# Revit family: Plumbing-Soap-Dispensers-Sloan-Valve-ESD-250
name_source: partatom
category: Specialty Equipment
units: mm (PartAtom-declared; Revit-internal decimal feet)

## family parameters
Cut with Voids When Loaded = No
Host = Face
OmniClass Number = 23.40.20.21.34
Part Type = Normal
Room Calculation Point = No
Round Connector Dimension = Use Diameter
Shared = No

## types (1)
- ESD-250-CP
    Assembly Code = D2010
    CW Connection = Yes
    Default Elevation = 0 "
    Depth = 5.38 "
    Description = Optima® Deck-Mounted Liquid Soap Dispenser, Polished Chrome Finish
    Edition number = 1
    HW Connection = Yes
    Height = 4.25 "
    Keynote = 15410
    Manufacturer = Sloan Valve
    Model = ESD-250-CP
    Part Number = 3346050
    Product Material = Sloan Valve - Finish - Polished Chrome
    URL = www.sloanvalve.com
    Vent Connection = No
    Waste Connection = No
    Width = 1.8 "

## geometry (parser evidence)
native form markers: Sweep x7
no freeform markers — native parametric forms only
